# Revit family: Progressive Safety Gear
name_source: partatom
category: Generic Models
units: mm (PartAtom-declared; Revit-internal decimal feet)

## family parameters
Always vertical = Yes
Can host rebar = No
Cut with Voids When Loaded = No
Maintain Annotation Orientation = No
Part Type = Normal
Room Calculation Point = No
Round Connector Dimension = Use Diameter
Shared = No
Work Plane-Based = No

## types (1)
- Progressive Safety Gear
    Default Elevation = 0 mm  [stored 0 ft]
    GuideRailSlot_Depth = 100 mm  [stored 0.328084 ft]
    GuideRailSlot_Width = 45 mm  [stored 0.147638 ft]
    Height = 280 mm  [stored 0.918635 ft]
    Length = 125 mm  [stored 0.410105 ft]
    SafetyGearType = Instantaneous
    SafetyGear_RatedSpeed = 1.0 m/s
    Width = 225 mm  [stored 0.738189 ft]

note: [stored X ft] marks values corroborated as IEEE doubles in the binary element streams (Revit-internal decimal feet)

## geometry (parser evidence)
native form markers: Sweep x3
no freeform markers — native parametric forms only
